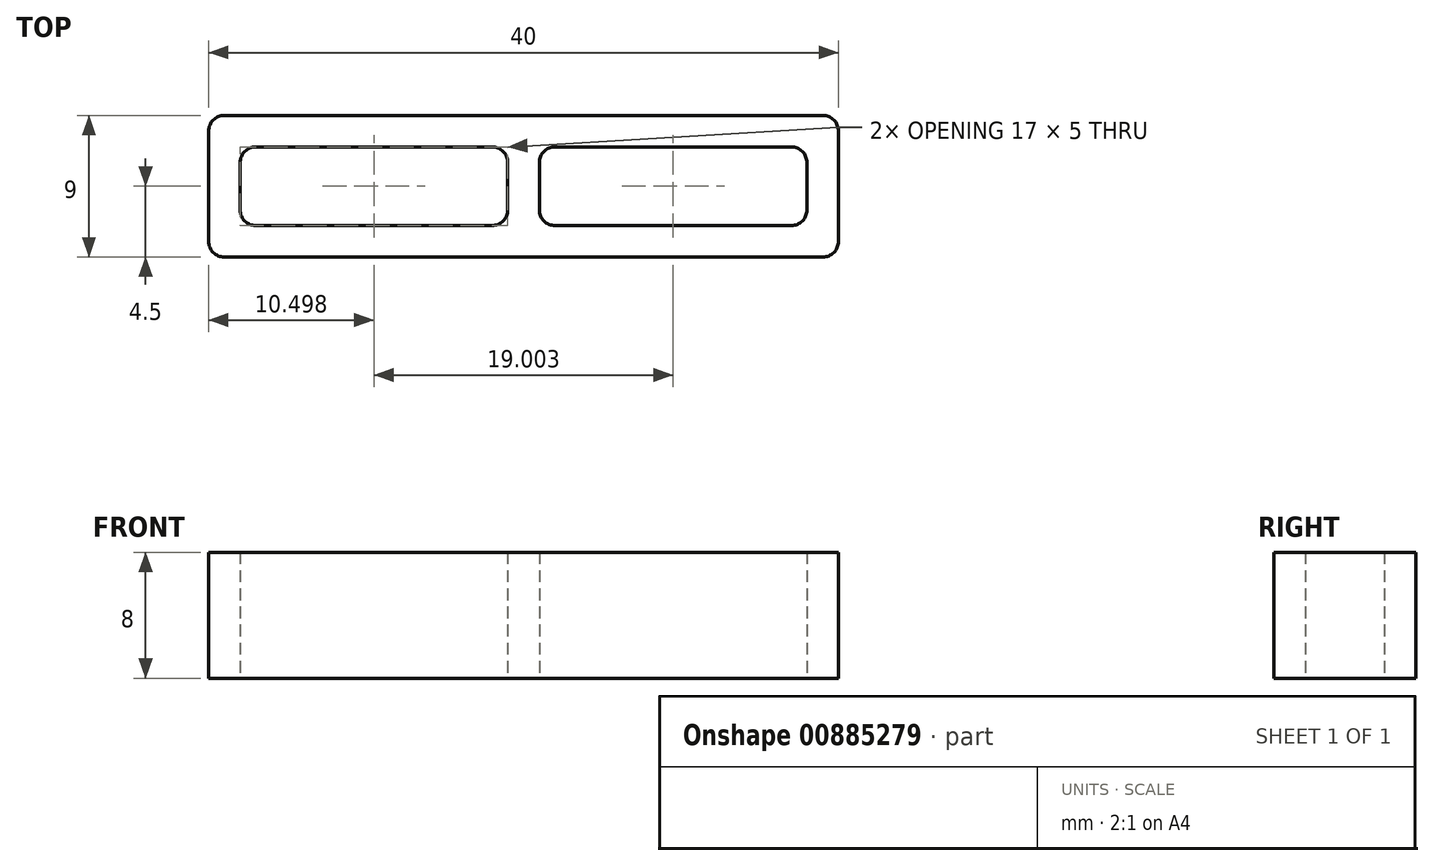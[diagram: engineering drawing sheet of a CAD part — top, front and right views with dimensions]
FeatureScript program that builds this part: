
annotation { "Feature Type Name" : "Feature", "Feature Type Description" : "" }
export const myFeature = defineFeature(function(context is Context, id is Id, definition is map)
    precondition{}
    {
        {
            var Q0;
            Q0=qCreatedBy(makeId("Top.planeOp"),FACE);
            var sketch = newSketch(context, id + "F0", { "sketchPlane" : qUnion([Q0])});
            skLineSegment(sketch, "E0.bottom", {"start": v(20, 4.5) * mm, "end": v(-20, 4.5) * mm});
            skLineSegment(sketch, "E0.top", {"start": v(20, -4.5) * mm, "end": v(-20, -4.5) * mm});
            skLineSegment(sketch, "E0.left", {"start": v(20, 4.5) * mm, "end": v(20, -4.5) * mm});
            skLineSegment(sketch, "E0.right", {"start": v(-20, 4.5) * mm, "end": v(-20, -4.5) * mm});
            skPoint(sketch, "E0.middle", {"position": v(0, 0) * mm});
            skLineSegment(sketch, "E1.bottom", {"start": v(18, 2.5) * mm, "end": v(1, 2.5) * mm});
            skLineSegment(sketch, "E1.top", {"start": v(18, -2.5) * mm, "end": v(1, -2.5) * mm});
            skLineSegment(sketch, "E1.left", {"start": v(18, 2.5) * mm, "end": v(18, -2.5) * mm});
            skLineSegment(sketch, "E1.right", {"start": v(-18, 2.5) * mm, "end": v(-18, -2.5) * mm});
            skLineSegment(sketch, "E2.left", {"start": v(1, 2.5) * mm, "end": v(1, -2.5) * mm});
            skLineSegment(sketch, "E2.right", {"start": v(-1, 2.5) * mm, "end": v(-1, -2.5) * mm});
            skLineSegment(sketch, "E3.trimOffspring", {"start": v(-1, 2.5) * mm, "end": v(-18, 2.5) * mm});
            skLineSegment(sketch, "E4.trimOffspring", {"start": v(-1, -2.5) * mm, "end": v(-18, -2.5) * mm});
            skSolve(sketch);
        }
        {
            var Q0;
            Q0 = qSketchRegion(id + "F0", true);
            extrude(context, id + "F1", {"entities" : qUnion([Q0]), "depth" : 8 * mm, "offsetDistance" : 25.4 * mm});
        }
        {
            var Q0;
            Q0=makeQuery(id+"F1.opExtrude","SWEPT_EDGE",EDGE,{"disambiguationData":[OSD([sQuery(id+"F0.wireOp",EDGE,"E0.top"),sQuery(id+"F0.wireOp",EDGE,"E0.right")])]});
            var Q1;
            Q1=makeQuery(id+"F1.opExtrude","SWEPT_EDGE",EDGE,{"disambiguationData":[OSD([sQuery(id+"F0.wireOp",EDGE,"E0.bottom"),sQuery(id+"F0.wireOp",EDGE,"E0.right")])]});
            var Q2;
            Q2=makeQuery(id+"F1.opExtrude","SWEPT_EDGE",EDGE,{"disambiguationData":[OSD([sQuery(id+"F0.wireOp",EDGE,"E0.top"),sQuery(id+"F0.wireOp",EDGE,"E0.left")])]});
            var Q3;
            Q3=makeQuery(id+"F1.opExtrude","SWEPT_EDGE",EDGE,{"disambiguationData":[OSD([sQuery(id+"F0.wireOp",EDGE,"E0.bottom"),sQuery(id+"F0.wireOp",EDGE,"E0.left")])]});
            fillet(context, id + "F2", {"entities" : qUnion([Q0, Q1, Q2, Q3]), "radius" : 1 * mm, "tangentPropagation" : true, "allowEdgeOverflow" : false});
        }
        {
            var Q0;
            Q0=makeQuery(id+"F1.opExtrude","SWEPT_EDGE",EDGE,{"disambiguationData":[OSD([sQuery(id+"F0.wireOp",EDGE,"E1.top"),sQuery(id+"F0.wireOp",EDGE,"E2.left")])]});
            var Q1;
            Q1=makeQuery(id+"F1.opExtrude","SWEPT_EDGE",EDGE,{"disambiguationData":[OSD([sQuery(id+"F0.wireOp",EDGE,"E1.bottom"),sQuery(id+"F0.wireOp",EDGE,"E2.left")])]});
            var Q2;
            Q2=makeQuery(id+"F1.opExtrude","SWEPT_EDGE",EDGE,{"disambiguationData":[OSD([sQuery(id+"F0.wireOp",EDGE,"E2.right"),sQuery(id+"F0.wireOp",EDGE,"E3.trimOffspring")])]});
            var Q3;
            Q3=makeQuery(id+"F1.opExtrude","SWEPT_EDGE",EDGE,{"disambiguationData":[OSD([sQuery(id+"F0.wireOp",EDGE,"E2.right"),sQuery(id+"F0.wireOp",EDGE,"E4.trimOffspring")])]});
            var Q4;
            Q4=makeQuery(id+"F1.opExtrude","SWEPT_EDGE",EDGE,{"disambiguationData":[OSD([sQuery(id+"F0.wireOp",EDGE,"E1.right"),sQuery(id+"F0.wireOp",EDGE,"E4.trimOffspring")])]});
            var Q5;
            Q5=makeQuery(id+"F1.opExtrude","SWEPT_EDGE",EDGE,{"disambiguationData":[OSD([sQuery(id+"F0.wireOp",EDGE,"E1.right"),sQuery(id+"F0.wireOp",EDGE,"E3.trimOffspring")])]});
            var Q6;
            Q6=makeQuery(id+"F1.opExtrude","SWEPT_EDGE",EDGE,{"disambiguationData":[OSD([sQuery(id+"F0.wireOp",EDGE,"E1.bottom"),sQuery(id+"F0.wireOp",EDGE,"E1.left")])]});
            var Q7;
            Q7=makeQuery(id+"F1.opExtrude","SWEPT_EDGE",EDGE,{"disambiguationData":[OSD([sQuery(id+"F0.wireOp",EDGE,"E1.top"),sQuery(id+"F0.wireOp",EDGE,"E1.left")])]});
            fillet(context, id + "F3", {"entities" : qUnion([Q0, Q1, Q2, Q3, Q4, Q5, Q6, Q7]), "radius" : 1 * mm, "tangentPropagation" : true, "allowEdgeOverflow" : false});
        }
    });
